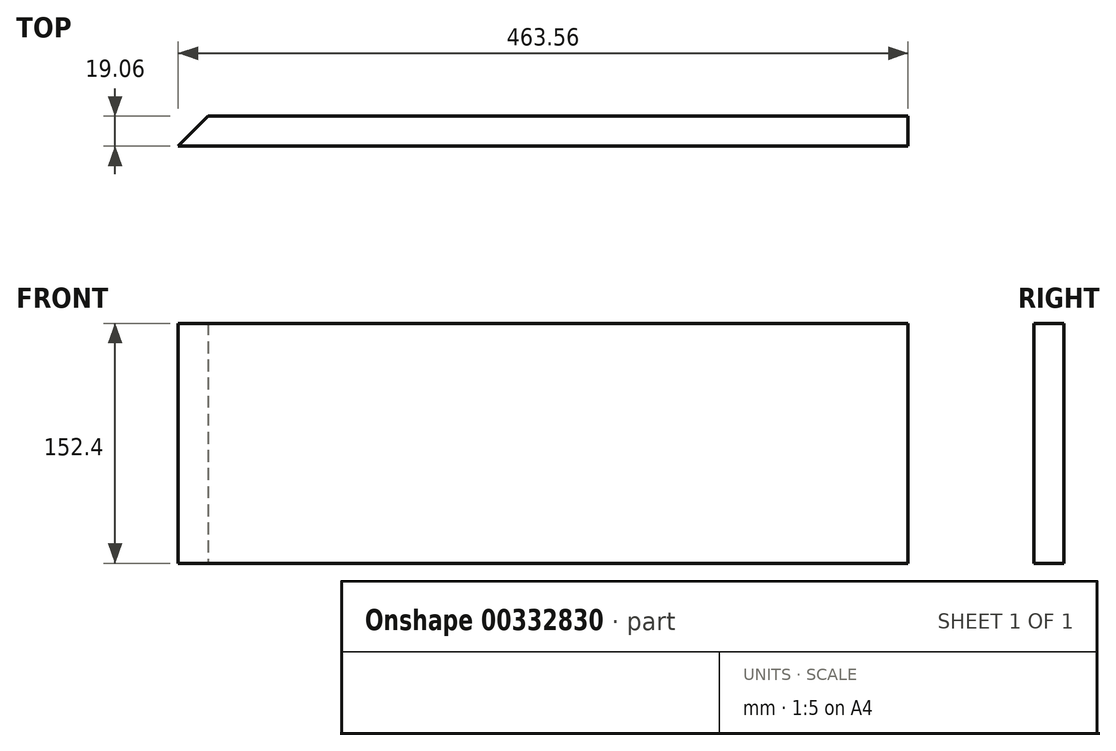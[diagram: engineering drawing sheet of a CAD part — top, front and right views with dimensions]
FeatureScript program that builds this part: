
annotation { "Feature Type Name" : "Feature", "Feature Type Description" : "" }
export const myFeature = defineFeature(function(context is Context, id is Id, definition is map)
    precondition{}
    {
        {
            var Q0;
            Q0=qCreatedBy(makeId("Top.planeOp"),FACE);
            var sketch = newSketch(context, id + "F0", { "sketchPlane" : qUnion([Q0])});
            skLineSegment(sketch, "E0.bottom", {"start": v(-231.78, -9.53) * mm, "end": v(231.77, -9.53) * mm});
            skLineSegment(sketch, "E0.top", {"start": v(-212.73, 9.52) * mm, "end": v(231.78, 9.52) * mm});
            skLineSegment(sketch, "E0.right", {"start": v(231.77, -9.53) * mm, "end": v(231.78, 9.52) * mm});
            skPoint(sketch, "E0.middle", {"position": v(0, 0) * mm});
            skLineSegment(sketch, "E1", {"start": v(-231.78, -9.53) * mm, "end": v(-212.73, 9.52) * mm});
            skPoint(sketch, "E0.left.end.orphan", {"position": v(-231.77, 9.52) * mm});
            skSolve(sketch);
        }
        {
            var Q0;
            Q0=qSketchRegion(id+"F0",true);
            extrude(context, id + "F1", {"entities" : qUnion([Q0]), "depth" : 152.4 * mm});
        }
    });
